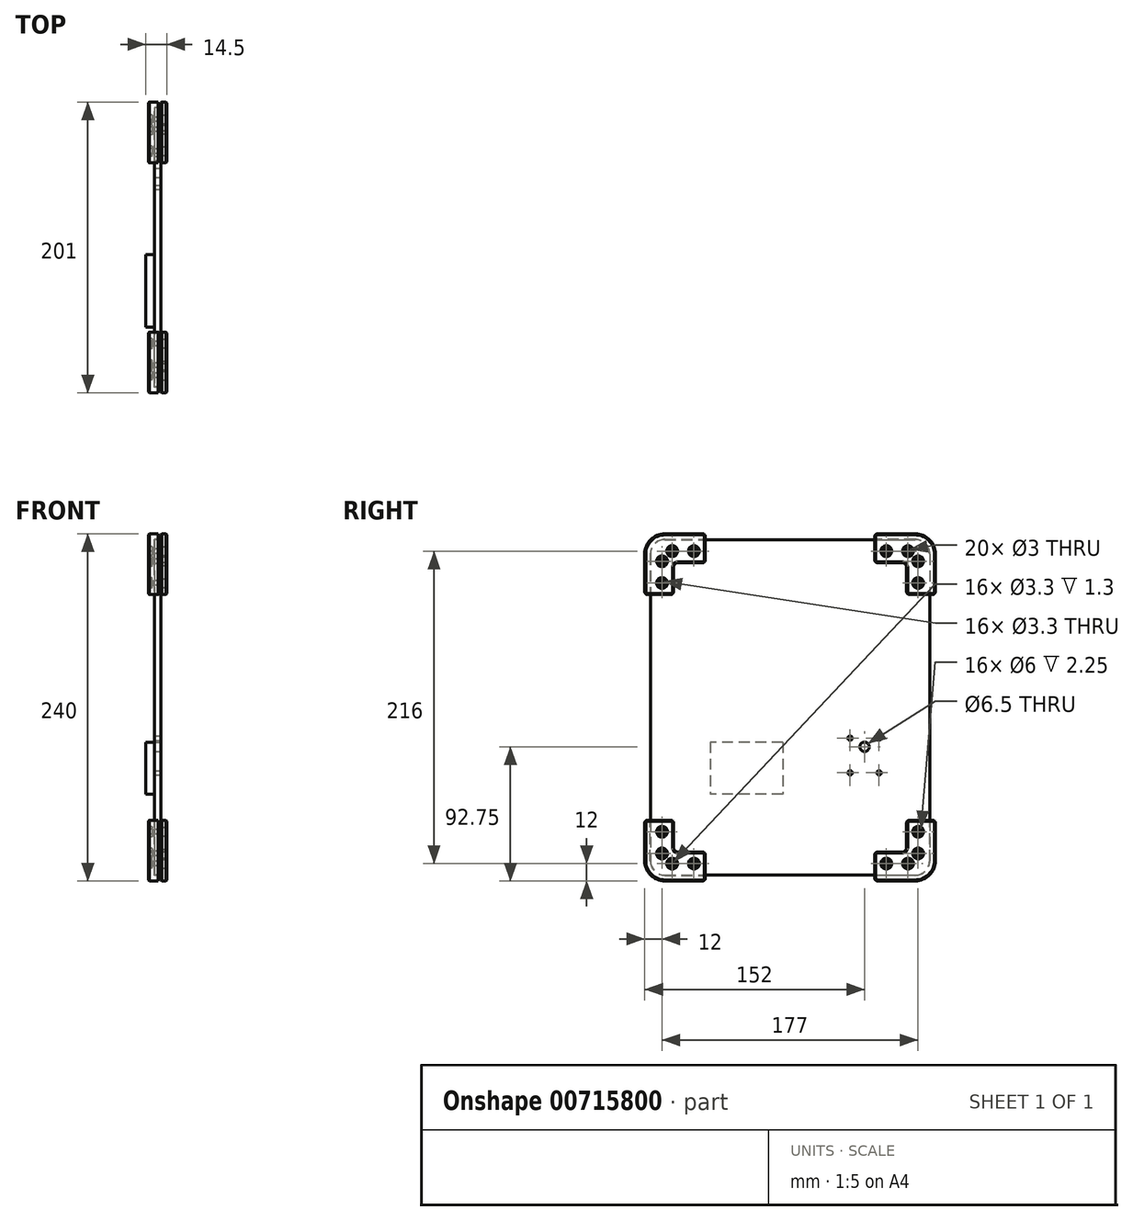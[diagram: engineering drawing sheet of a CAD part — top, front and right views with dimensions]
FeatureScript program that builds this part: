
annotation { "Feature Type Name" : "Feature", "Feature Type Description" : "" }
export const myFeature = defineFeature(function(context is Context, id is Id, definition is map)
    precondition{}
    {
        {
            assignVariable(context, id + "F0", {"name" : "thickness", "anyValue" : 4.5});
        }
        {
            assignVariable(context, id + "F1", {"name" : "m3_printed", "anyValue" : 3.3});
        }
        {
            assignVariable(context, id + "F2", {"name" : "m3_head", "anyValue" : 6});
        }
        {
            var Q0;
            Q0=qCreatedBy(makeId("Right.planeOp"),FACE);
            var sketch = newSketch(context, id + "F3", { "sketchPlane" : qUnion([Q0])});
            skLineSegment(sketch, "E0.bottom", {"start": v(-86.5, 116) * mm, "end": v(86.5, 116) * mm});
            skLineSegment(sketch, "E0.top", {"start": v(-86.5, -116) * mm, "end": v(86.5, -116) * mm});
            skLineSegment(sketch, "E0.left", {"start": v(-96.5, 106) * mm, "end": v(-96.5, -106) * mm});
            skLineSegment(sketch, "E0.right", {"start": v(96.5, 106) * mm, "end": v(96.5, -106) * mm});
            skPoint(sketch, "E0.middle", {"position": v(0, 0) * mm});
            skPoint(sketch, "E1.visualSharp", {"position": v(-96.5, 116) * mm});
            skArc(sketch, "E1.filletArc", {"start": v(-86.5, 116) * mm, "mid": v(-93.57, 113.07) * mm, "end": v(-96.5, 106) * mm});
            skPoint(sketch, "E2.visualSharp", {"position": v(96.5, 116) * mm});
            skArc(sketch, "E2.filletArc", {"start": v(96.5, 106) * mm, "mid": v(93.57, 113.07) * mm, "end": v(86.5, 116) * mm});
            skPoint(sketch, "E3.visualSharp", {"position": v(96.5, -116) * mm});
            skArc(sketch, "E3.filletArc", {"start": v(86.5, -116) * mm, "mid": v(93.57, -113.07) * mm, "end": v(96.5, -106) * mm});
            skPoint(sketch, "E4.visualSharp", {"position": v(-96.5, -116) * mm});
            skArc(sketch, "E4.filletArc", {"start": v(-96.5, -106) * mm, "mid": v(-93.57, -113.07) * mm, "end": v(-86.5, -116) * mm});
            skSolve(sketch);
        }
        {
            var Q0;
            Q0 = qSketchRegion(id + "F3", true);
            extrude(context, id + "F4", {"entities" : qUnion([Q0]), "endBound" : BoundingType.SYMMETRIC, "depth" : (getVariable(context, 'thickness')) * mm, "offsetDistance" : 25 * mm});
        }
        {
            var Q0;
            Q0=qCreatedBy(makeId("Right.planeOp"),FACE);
            var sketch = newSketch(context, id + "F5", { "sketchPlane" : qUnion([Q0])});
            skCircle(sketch, "E5", {"center": v(-66.5, 108) * mm, "radius": 1.5 * mm});
            skCircle(sketch, "E6", {"center": v(-81.5, 108) * mm, "radius": 1.5 * mm});
            skCircle(sketch, "E7", {"center": v(-88.5, 101) * mm, "radius": 1.5 * mm});
            skCircle(sketch, "E8", {"center": v(-88.5, 86) * mm, "radius": 1.5 * mm});
            skCircle(sketch, "E9.MirrorC", {"center": v(66.5, 108) * mm, "radius": 1.5 * mm});
            skCircle(sketch, "E10.MirrorC", {"center": v(81.5, 108) * mm, "radius": 1.5 * mm});
            skCircle(sketch, "E11.MirrorC", {"center": v(88.5, 101) * mm, "radius": 1.5 * mm});
            skCircle(sketch, "E12.MirrorC", {"center": v(88.5, 86) * mm, "radius": 1.5 * mm});
            skCircle(sketch, "E13.MirrorC", {"center": v(88.5, -101) * mm, "radius": 1.5 * mm});
            skCircle(sketch, "E14.MirrorC", {"center": v(88.5, -86) * mm, "radius": 1.5 * mm});
            skCircle(sketch, "E15.MirrorC", {"center": v(81.5, -108) * mm, "radius": 1.5 * mm});
            skCircle(sketch, "E16.MirrorC", {"center": v(66.5, -108) * mm, "radius": 1.5 * mm});
            skCircle(sketch, "E17.MirrorC", {"center": v(-88.5, -86) * mm, "radius": 1.5 * mm});
            skCircle(sketch, "E18.MirrorC", {"center": v(-88.5, -101) * mm, "radius": 1.5 * mm});
            skCircle(sketch, "E19.MirrorC", {"center": v(-81.5, -108) * mm, "radius": 1.5 * mm});
            skCircle(sketch, "E20.MirrorC", {"center": v(-66.5, -108) * mm, "radius": 1.5 * mm});
            skLineSegment(sketch, "E21", {"start": v(-66.5, 108) * mm, "end": v(-81.5, 108) * mm, "construction": true});
            skLineSegment(sketch, "E22", {"start": v(-81.5, 108) * mm, "end": v(-96.5, 108) * mm, "construction": true});
            skLineSegment(sketch, "E23", {"start": v(-88.5, 86) * mm, "end": v(-88.5, 101) * mm, "construction": true});
            skLineSegment(sketch, "E24", {"start": v(-88.5, 101) * mm, "end": v(-88.5, 116) * mm, "construction": true});
            skLineSegment(sketch, "E25", {"start": v(-81.5, 108) * mm, "end": v(-81.5, 116) * mm, "construction": true});
            skLineSegment(sketch, "E26", {"start": v(-88.5, 101) * mm, "end": v(-96.5, 101) * mm, "construction": true});
            skSolve(sketch);
        }
        {
            var Q0;
            Q0 = qSketchRegion(id + "F5", true);
            extrude(context, id + "F6", {"entities" : qUnion([Q0]), "operationType" : NewBodyOperationType.REMOVE, "endBound" : BoundingType.SYMMETRIC, "depth" : 5 * mm, "offsetDistance" : 25 * mm});
        }
        {
            var Q0;
            Q0=makeQuery(id+"F4.opExtrude","CAP_FACE",FACE,{"disambiguationData":[OSD([sQuery(id+"F3.wireOp",EDGE,"E0.bottom"),sQuery(id+"F3.wireOp",EDGE,"E0.top"),sQuery(id+"F3.wireOp",EDGE,"E0.left"),sQuery(id+"F3.wireOp",EDGE,"E0.right"),sQuery(id+"F3.wireOp",EDGE,"E1.filletArc"),sQuery(id+"F3.wireOp",EDGE,"E2.filletArc"),sQuery(id+"F3.wireOp",EDGE,"E3.filletArc"),sQuery(id+"F3.wireOp",EDGE,"E4.filletArc")])],"isStart":false});
            var sketch = newSketch(context, id + "F7", { "sketchPlane" : qUnion([Q0])});
            skLineSegment(sketch, "E27", {"start": v(-58.5, 120) * mm, "end": v(-86.5, 120) * mm});
            skLineSegment(sketch, "E28", {"start": v(-100.5, 106) * mm, "end": v(-100.5, 78) * mm});
            skLineSegment(sketch, "E29", {"start": v(-100.5, 78) * mm, "end": v(-80.5, 78) * mm});
            skLineSegment(sketch, "E30", {"start": v(-80.5, 78) * mm, "end": v(-80.5, 97) * mm});
            skLineSegment(sketch, "E31", {"start": v(-77.5, 100) * mm, "end": v(-58.5, 100) * mm});
            skLineSegment(sketch, "E32", {"start": v(-58.5, 100) * mm, "end": v(-58.5, 120) * mm});
            skPoint(sketch, "E33.visualSharp", {"position": v(-100.5, 120) * mm});
            skArc(sketch, "E33.filletArc", {"start": v(-86.5, 120) * mm, "mid": v(-96.4, 115.9) * mm, "end": v(-100.5, 106) * mm});
            skPoint(sketch, "E34.visualSharp", {"position": v(-80.5, 100) * mm});
            skArc(sketch, "E34.filletArc", {"start": v(-77.5, 100) * mm, "mid": v(-79.62, 99.12) * mm, "end": v(-80.5, 97) * mm});
            skLineSegment(sketch, "E35", {"start": v(-66.5, 100) * mm, "end": v(-66.5, 108) * mm, "construction": true});
            skLineSegment(sketch, "E36", {"start": v(-66.5, 108) * mm, "end": v(-58.5, 108) * mm, "construction": true});
            skLineSegment(sketch, "E37", {"start": v(-88.5, 86) * mm, "end": v(-88.5, 78) * mm, "construction": true});
            skLineSegment(sketch, "E38", {"start": v(-88.5, 86) * mm, "end": v(-80.5, 86) * mm, "construction": true});
            skPoint(sketch, "E39", {"position": v(-81.5, 108) * mm});
            skPoint(sketch, "E40", {"position": v(-88.5, 101) * mm});
            skPoint(sketch, "E41", {"position": v(-88.5, 86) * mm});
            skPoint(sketch, "E42", {"position": v(-66.5, 108) * mm});
            skSolve(sketch);
        }
        {
            var Q0;
            Q0 = qSketchRegion(id + "F7", true);
            extrude(context, id + "F8", {"entities" : qUnion([Q0]), "depth" : 4 * mm, "offsetDistance" : 25 * mm});
        }
        {
            var Q0;
            Q0=makeQuery(id+"F4.opExtrude","CAP_FACE",FACE,{"disambiguationData":[OSD([sQuery(id+"F3.wireOp",EDGE,"E0.bottom"),sQuery(id+"F3.wireOp",EDGE,"E0.top"),sQuery(id+"F3.wireOp",EDGE,"E0.left"),sQuery(id+"F3.wireOp",EDGE,"E0.right"),sQuery(id+"F3.wireOp",EDGE,"E1.filletArc"),sQuery(id+"F3.wireOp",EDGE,"E2.filletArc"),sQuery(id+"F3.wireOp",EDGE,"E3.filletArc"),sQuery(id+"F3.wireOp",EDGE,"E4.filletArc")])],"isStart":true});
            var sketch = newSketch(context, id + "F9", { "sketchPlane" : qUnion([Q0])});
            skLineSegment(sketch, "E43.0", {"start": v(58.5, 100) * mm, "end": v(58.5, 120) * mm});
            skLineSegment(sketch, "E43.1", {"start": v(77.5, 100) * mm, "end": v(58.5, 100) * mm});
            skLineSegment(sketch, "E43.2", {"start": v(58.5, 120) * mm, "end": v(86.5, 120) * mm});
            skArc(sketch, "E43.3", {"start": v(77.5, 100) * mm, "mid": v(79.62, 99.12) * mm, "end": v(80.5, 97) * mm});
            skArc(sketch, "E43.4", {"start": v(86.5, 120) * mm, "mid": v(96.4, 115.9) * mm, "end": v(100.5, 106) * mm});
            skLineSegment(sketch, "E43.5", {"start": v(100.5, 106) * mm, "end": v(100.5, 78) * mm});
            skLineSegment(sketch, "E43.6", {"start": v(100.5, 78) * mm, "end": v(80.5, 78) * mm});
            skLineSegment(sketch, "E43.7", {"start": v(80.5, 78) * mm, "end": v(80.5, 97) * mm});
            skSolve(sketch);
        }
        {
            var Q0;
            Q0 = qSketchRegion(id + "F9", true);
            extrude(context, id + "F10", {"entities" : qUnion([Q0]), "depth" : 4 * mm, "offsetDistance" : 25 * mm});
        }
        {
            var Q0;
            Q0=makeQuery(id+"F10.opExtrude","CAP_FACE",FACE,{"disambiguationData":[OSD([sQuery(id+"F9.wireOp",EDGE,"E43.0"),sQuery(id+"F9.wireOp",EDGE,"E43.1"),sQuery(id+"F9.wireOp",EDGE,"E43.2"),sQuery(id+"F9.wireOp",EDGE,"E43.3"),sQuery(id+"F9.wireOp",EDGE,"E43.4"),sQuery(id+"F9.wireOp",EDGE,"E43.5"),sQuery(id+"F9.wireOp",EDGE,"E43.6"),sQuery(id+"F9.wireOp",EDGE,"E43.7")])],"isStart":true});
            var sketch = newSketch(context, id + "F11", { "sketchPlane" : qUnion([Q0])});
            skLineSegment(sketch, "E44.0", {"start": v(-100.5, 78) * mm, "end": v(-96.6, 78) * mm});
            skLineSegment(sketch, "E44.1", {"start": v(-58.5, 116.1) * mm, "end": v(-58.5, 120) * mm});
            skLineSegment(sketch, "E44.2", {"start": v(-58.5, 120) * mm, "end": v(-86.5, 120) * mm});
            skArc(sketch, "E44.3", {"start": v(-86.5, 120) * mm, "mid": v(-96.4, 115.9) * mm, "end": v(-100.5, 106) * mm});
            skLineSegment(sketch, "E44.4", {"start": v(-100.5, 106) * mm, "end": v(-100.5, 78) * mm});
            skLineSegment(sketch, "E45.0", {"start": v(-96.6, 106) * mm, "end": v(-96.6, 78) * mm});
            skArc(sketch, "E45.1", {"start": v(-86.5, 116.1) * mm, "mid": v(-93.64, 113.14) * mm, "end": v(-96.6, 106) * mm});
            skLineSegment(sketch, "E45.2", {"start": v(-86.5, 116.1) * mm, "end": v(-58.5, 116.1) * mm});
            skSolve(sketch);
        }
        {
            var Q0;
            Q0 = qSketchRegion(id + "F11", true);
            extrude(context, id + "F12", {"entities" : qUnion([Q0]), "operationType" : NewBodyOperationType.ADD, "depth" : 2.6 * mm, "offsetDistance" : 25 * mm});
        }
        {
            var Q0;
            Q0=makeQuery(id+"F8.opExtrude","CAP_FACE",FACE,{"disambiguationData":[OSD([sQuery(id+"F7.wireOp",EDGE,"E27"),sQuery(id+"F7.wireOp",EDGE,"E28"),sQuery(id+"F7.wireOp",EDGE,"E29"),sQuery(id+"F7.wireOp",EDGE,"E30"),sQuery(id+"F7.wireOp",EDGE,"E31"),sQuery(id+"F7.wireOp",EDGE,"E32"),sQuery(id+"F7.wireOp",EDGE,"E33.filletArc"),sQuery(id+"F7.wireOp",EDGE,"E34.filletArc")])],"isStart":false});
            var sketch = newSketch(context, id + "F13", { "sketchPlane" : qUnion([Q0])});
            skPoint(sketch, "E46", {"position": v(-81.5, 108) * mm});
            skPoint(sketch, "E47", {"position": v(-88.5, 101) * mm});
            skPoint(sketch, "E48", {"position": v(-88.5, 86) * mm});
            skPoint(sketch, "E49", {"position": v(-66.5, 108) * mm});
            skSolve(sketch);
        }
        {
            var Q0;
            Q0=sQuery(id+"F13.wireOp",VERTEX,"E48");
            var Q1;
            Q1=sQuery(id+"F13.wireOp",VERTEX,"E47");
            var Q2;
            Q2=sQuery(id+"F13.wireOp",VERTEX,"E46");
            var Q3;
            Q3=sQuery(id+"F13.wireOp",VERTEX,"E49");
            var Q4;
            Q4=makeQuery(id+"F8.opExtrude","SWEPT_BODY",BODY,{"disambiguationData":[OSD([sQuery(id+"F7.wireOp",EDGE,"E27"),sQuery(id+"F7.wireOp",EDGE,"E28"),sQuery(id+"F7.wireOp",EDGE,"E29"),sQuery(id+"F7.wireOp",EDGE,"E30"),sQuery(id+"F7.wireOp",EDGE,"E31"),sQuery(id+"F7.wireOp",EDGE,"E32"),sQuery(id+"F7.wireOp",EDGE,"E33.filletArc"),sQuery(id+"F7.wireOp",EDGE,"E34.filletArc")])]});
            hole(context, id + "F14", {"style" : HoleStyle.C_BORE, "endStyle" : HoleEndStyle.THROUGH, "holeDiameter" : (getVariable(context, 'm3_printed')) * mm, "cBoreDiameter" : (getVariable(context, 'm3_head')) * mm, "cBoreDepth" : 3 * mm, "majorDiameter" : 5 * mm, "isTappedThrough" : true, "tappedDepth" : 12 * mm, "tapClearance" : 3, "locations" : qUnion([Q0, Q1, Q2, Q3]), "scope" : qUnion([Q4])});
        }
        {
            var Q0;
            Q0=makeQuery(id+"F8.opExtrude","SWEPT_EDGE",EDGE,{"disambiguationData":[OSD([sQuery(id+"F7.wireOp",EDGE,"E31"),sQuery(id+"F7.wireOp",EDGE,"E32")])]});
            var Q1;
            Q1=makeQuery(id+"F8.opExtrude","SWEPT_EDGE",EDGE,{"disambiguationData":[OSD([sQuery(id+"F7.wireOp",EDGE,"E29"),sQuery(id+"F7.wireOp",EDGE,"E30")])]});
            var Q2;
            Q2=makeQuery(id+"F8.opExtrude","SWEPT_EDGE",EDGE,{"disambiguationData":[OSD([sQuery(id+"F7.wireOp",EDGE,"E27"),sQuery(id+"F7.wireOp",EDGE,"E32")])]});
            var Q3;
            Q3=makeQuery(id+"F8.opExtrude","SWEPT_EDGE",EDGE,{"disambiguationData":[OSD([sQuery(id+"F7.wireOp",EDGE,"E28"),sQuery(id+"F7.wireOp",EDGE,"E29")])]});
            fillet(context, id + "F15", {"entities" : qUnion([Q0, Q1, Q2, Q3]), "radius" : 2 * mm, "tangentPropagation" : true, "allowEdgeOverflow" : false});
        }
        {
            var Q0;
            Q0=makeQuery(id+"F8.opExtrude","CAP_FACE",FACE,{"disambiguationData":[OSD([sQuery(id+"F7.wireOp",EDGE,"E27"),sQuery(id+"F7.wireOp",EDGE,"E28"),sQuery(id+"F7.wireOp",EDGE,"E29"),sQuery(id+"F7.wireOp",EDGE,"E30"),sQuery(id+"F7.wireOp",EDGE,"E31"),sQuery(id+"F7.wireOp",EDGE,"E32"),sQuery(id+"F7.wireOp",EDGE,"E33.filletArc"),sQuery(id+"F7.wireOp",EDGE,"E34.filletArc")])],"isStart":false});
            chamfer(context, id + "F16", {"entities" : qUnion([Q0]), "width" : .75 * mm, "tangentPropagation" : true});
        }
        {
            var Q0;
            Q0=makeQuery(id+"F8.opExtrude","CAP_FACE",FACE,{"disambiguationData":[OSD([sQuery(id+"F7.wireOp",EDGE,"E27"),sQuery(id+"F7.wireOp",EDGE,"E28"),sQuery(id+"F7.wireOp",EDGE,"E29"),sQuery(id+"F7.wireOp",EDGE,"E30"),sQuery(id+"F7.wireOp",EDGE,"E31"),sQuery(id+"F7.wireOp",EDGE,"E32"),sQuery(id+"F7.wireOp",EDGE,"E33.filletArc"),sQuery(id+"F7.wireOp",EDGE,"E34.filletArc")])],"isStart":true});
            chamfer(context, id + "F17", {"entities" : qUnion([Q0]), "width" : .5 * mm, "tangentPropagation" : true});
        }
        {
            var Q0;
            Q0=makeQuery(id+"F10.opExtrude","CAP_FACE",FACE,{"disambiguationData":[OSD([sQuery(id+"F9.wireOp",EDGE,"E43.0"),sQuery(id+"F9.wireOp",EDGE,"E43.1"),sQuery(id+"F9.wireOp",EDGE,"E43.2"),sQuery(id+"F9.wireOp",EDGE,"E43.3"),sQuery(id+"F9.wireOp",EDGE,"E43.4"),sQuery(id+"F9.wireOp",EDGE,"E43.5"),sQuery(id+"F9.wireOp",EDGE,"E43.6"),sQuery(id+"F9.wireOp",EDGE,"E43.7")])],"isStart":true});
            var sketch = newSketch(context, id + "F18", { "sketchPlane" : qUnion([Q0])});
            skPoint(sketch, "E50", {"position": v(-88.5, 86) * mm});
            skPoint(sketch, "E51", {"position": v(-88.5, 101) * mm});
            skPoint(sketch, "E52", {"position": v(-81.5, 108) * mm});
            skPoint(sketch, "E53", {"position": v(-66.5, 108) * mm});
            skSolve(sketch);
        }
        {
            var Q0;
            Q0=sQuery(id+"F18.wireOp",VERTEX,"E51");
            var Q1;
            Q1=sQuery(id+"F18.wireOp",VERTEX,"E50");
            var Q2;
            Q2=sQuery(id+"F18.wireOp",VERTEX,"E52");
            var Q3;
            Q3=sQuery(id+"F18.wireOp",VERTEX,"E53");
            var Q4;
            Q4=makeQuery(id+"F10.opExtrude","SWEPT_BODY",BODY,{"disambiguationData":[OSD([sQuery(id+"F9.wireOp",EDGE,"E43.0"),sQuery(id+"F9.wireOp",EDGE,"E43.1"),sQuery(id+"F9.wireOp",EDGE,"E43.2"),sQuery(id+"F9.wireOp",EDGE,"E43.3"),sQuery(id+"F9.wireOp",EDGE,"E43.4"),sQuery(id+"F9.wireOp",EDGE,"E43.5"),sQuery(id+"F9.wireOp",EDGE,"E43.6"),sQuery(id+"F9.wireOp",EDGE,"E43.7")])]});
            hole(context, id + "F19", {"style" : HoleStyle.SIMPLE, "endStyle" : HoleEndStyle.THROUGH, "holeDiameter" : (getVariable(context, 'm3_printed')) * mm, "majorDiameter" : 5 * mm, "isTappedThrough" : true, "tappedDepth" : 12 * mm, "tapClearance" : 3, "locations" : qUnion([Q0, Q1, Q2, Q3]), "scope" : qUnion([Q4])});
        }
        {
            var Q0;
            Q0=makeQuery(id+"F10.opExtrude","CAP_FACE",FACE,{"disambiguationData":[OSD([sQuery(id+"F9.wireOp",EDGE,"E43.0"),sQuery(id+"F9.wireOp",EDGE,"E43.1"),sQuery(id+"F9.wireOp",EDGE,"E43.2"),sQuery(id+"F9.wireOp",EDGE,"E43.3"),sQuery(id+"F9.wireOp",EDGE,"E43.4"),sQuery(id+"F9.wireOp",EDGE,"E43.5"),sQuery(id+"F9.wireOp",EDGE,"E43.6"),sQuery(id+"F9.wireOp",EDGE,"E43.7")])],"isStart":false});
            var sketch = newSketch(context, id + "F20", { "sketchPlane" : qUnion([Q0])});
            skCircle(sketch, "E54.cCircle", {"center": v(88.5, 86) * mm, "radius": 3.46 * mm, "construction": true});
            skLineSegment(sketch, "E54.0", {"start": v(85.5, 87.73) * mm, "end": v(88.5, 89.46) * mm});
            skLineSegment(sketch, "E54.1", {"start": v(88.5, 89.46) * mm, "end": v(91.5, 87.73) * mm});
            skLineSegment(sketch, "E54.2", {"start": v(91.5, 87.73) * mm, "end": v(91.5, 84.27) * mm});
            skLineSegment(sketch, "E54.3", {"start": v(91.5, 84.27) * mm, "end": v(88.5, 82.54) * mm});
            skLineSegment(sketch, "E54.4", {"start": v(88.5, 82.54) * mm, "end": v(85.5, 84.27) * mm});
            skLineSegment(sketch, "E54.5", {"start": v(85.5, 84.27) * mm, "end": v(85.5, 87.73) * mm});
            skCircle(sketch, "E55.cCircle", {"center": v(88.5, 101) * mm, "radius": 3.46 * mm, "construction": true});
            skLineSegment(sketch, "E55.0", {"start": v(85.5, 99.27) * mm, "end": v(85.5, 102.73) * mm});
            skLineSegment(sketch, "E55.1", {"start": v(85.5, 102.73) * mm, "end": v(88.5, 104.46) * mm});
            skLineSegment(sketch, "E55.2", {"start": v(88.5, 104.46) * mm, "end": v(91.5, 102.73) * mm});
            skLineSegment(sketch, "E55.3", {"start": v(91.5, 102.73) * mm, "end": v(91.5, 99.27) * mm});
            skLineSegment(sketch, "E55.4", {"start": v(91.5, 99.27) * mm, "end": v(88.5, 97.54) * mm});
            skLineSegment(sketch, "E55.5", {"start": v(88.5, 97.54) * mm, "end": v(85.5, 99.27) * mm});
            skCircle(sketch, "E56.cCircle", {"center": v(81.5, 108) * mm, "radius": 3.46 * mm, "construction": true});
            skLineSegment(sketch, "E56.0", {"start": v(79.77, 105) * mm, "end": v(78.04, 108) * mm});
            skLineSegment(sketch, "E56.1", {"start": v(78.04, 108) * mm, "end": v(79.77, 111) * mm});
            skLineSegment(sketch, "E56.2", {"start": v(79.77, 111) * mm, "end": v(83.23, 111) * mm});
            skLineSegment(sketch, "E56.3", {"start": v(83.23, 111) * mm, "end": v(84.96, 108) * mm});
            skLineSegment(sketch, "E56.4", {"start": v(84.96, 108) * mm, "end": v(83.23, 105) * mm});
            skLineSegment(sketch, "E56.5", {"start": v(83.23, 105) * mm, "end": v(79.77, 105) * mm});
            skCircle(sketch, "E57.cCircle", {"center": v(66.5, 108) * mm, "radius": 3.46 * mm, "construction": true});
            skLineSegment(sketch, "E57.0", {"start": v(68.23, 105) * mm, "end": v(64.77, 105) * mm});
            skLineSegment(sketch, "E57.1", {"start": v(64.77, 105) * mm, "end": v(63.04, 108) * mm});
            skLineSegment(sketch, "E57.2", {"start": v(63.04, 108) * mm, "end": v(64.77, 111) * mm});
            skLineSegment(sketch, "E57.3", {"start": v(64.77, 111) * mm, "end": v(68.23, 111) * mm});
            skLineSegment(sketch, "E57.4", {"start": v(68.23, 111) * mm, "end": v(69.96, 108) * mm});
            skLineSegment(sketch, "E57.5", {"start": v(69.96, 108) * mm, "end": v(68.23, 105) * mm});
            skSolve(sketch);
        }
        {
            var Q0;
            Q0 = qSketchRegion(id + "F20", true);
            extrude(context, id + "F21", {"entities" : qUnion([Q0]), "operationType" : NewBodyOperationType.REMOVE, "oppositeDirection" : true, "depth" : 2.5 * mm, "offsetDistance" : 25 * mm});
        }
        {
            var Q0;
            Q0=makeQuery(id+"F10.opExtrude","SWEPT_EDGE",EDGE,{"disambiguationData":[OSD([sQuery(id+"F9.wireOp",EDGE,"E43.0"),sQuery(id+"F9.wireOp",EDGE,"E43.1")])]});
            var Q1;
            Q1=makeQuery(id+"F10.opExtrude","SWEPT_EDGE",EDGE,{"disambiguationData":[OSD([sQuery(id+"F9.wireOp",EDGE,"E43.6"),sQuery(id+"F9.wireOp",EDGE,"E43.7")])]});
            var Q2;
            Q2=makeQuery(id+"F12.boolean.opBoolean","MERGE",EDGE,{"derivedFrom":[makeQuery(id+"F10.opExtrude","SWEPT_EDGE",EDGE,{"disambiguationData":[OSD([sQuery(id+"F9.wireOp",EDGE,"E43.5"),sQuery(id+"F9.wireOp",EDGE,"E43.6")])]}),makeQuery(id+"F12.opExtrude","SWEPT_EDGE",EDGE,{"disambiguationData":[OSD([sQuery(id+"F11.wireOp",EDGE,"E44.0"),sQuery(id+"F11.wireOp",EDGE,"E44.4")])]})]});
            var Q3;
            Q3=makeQuery(id+"F12.boolean.opBoolean","MERGE",EDGE,{"derivedFrom":[makeQuery(id+"F10.opExtrude","SWEPT_EDGE",EDGE,{"disambiguationData":[OSD([sQuery(id+"F9.wireOp",EDGE,"E43.0"),sQuery(id+"F9.wireOp",EDGE,"E43.2")])]}),makeQuery(id+"F12.opExtrude","SWEPT_EDGE",EDGE,{"disambiguationData":[OSD([sQuery(id+"F11.wireOp",EDGE,"E44.1"),sQuery(id+"F11.wireOp",EDGE,"E44.2")])]})]});
            fillet(context, id + "F22", {"entities" : qUnion([Q0, Q1, Q2, Q3]), "radius" : 2 * mm, "tangentPropagation" : true, "allowEdgeOverflow" : false});
        }
        {
            var Q0;
            Q0=makeQuery(id+"F10.opExtrude","CAP_FACE",FACE,{"disambiguationData":[OSD([sQuery(id+"F9.wireOp",EDGE,"E43.0"),sQuery(id+"F9.wireOp",EDGE,"E43.1"),sQuery(id+"F9.wireOp",EDGE,"E43.2"),sQuery(id+"F9.wireOp",EDGE,"E43.3"),sQuery(id+"F9.wireOp",EDGE,"E43.4"),sQuery(id+"F9.wireOp",EDGE,"E43.5"),sQuery(id+"F9.wireOp",EDGE,"E43.6"),sQuery(id+"F9.wireOp",EDGE,"E43.7")])],"isStart":false});
            chamfer(context, id + "F23", {"entities" : qUnion([Q0]), "width" : 0.5 * mm, "tangentPropagation" : true});
        }
        {
            var Q0;
            Q0=makeQuery(id+"F21.boolean.opBoolean","COPY",FACE,{"derivedFrom":makeQuery(id+"F21.opExtrude","CAP_FACE",FACE,{"disambiguationData":[OSD([sQuery(id+"F20.wireOp",EDGE,"E54.0"),sQuery(id+"F20.wireOp",EDGE,"E54.1"),sQuery(id+"F20.wireOp",EDGE,"E54.2"),sQuery(id+"F20.wireOp",EDGE,"E54.3"),sQuery(id+"F20.wireOp",EDGE,"E54.4"),sQuery(id+"F20.wireOp",EDGE,"E54.5")])],"isStart":false})});
            var sketch = newSketch(context, id + "F24", { "sketchPlane" : qUnion([Q0])});
            skCircle(sketch, "E58", {"center": v(88.5, 86) * mm, "radius": 1.65 * mm});
            skCircle(sketch, "E59", {"center": v(88.5, 101) * mm, "radius": 1.65 * mm});
            skCircle(sketch, "E60", {"center": v(81.5, 108) * mm, "radius": 1.65 * mm});
            skCircle(sketch, "E61", {"center": v(66.5, 108) * mm, "radius": 1.65 * mm});
            skSolve(sketch);
        }
        {
            var Q0;
            Q0 = qSketchRegion(id + "F24", true);
            extrude(context, id + "F25", {"entities" : qUnion([Q0]), "operationType" : NewBodyOperationType.ADD, "oppositeDirection" : true, "depth" : .2 * mm, "offsetDistance" : 25 * mm});
        }
        {
            var Q0;
            Q0=makeQuery(id+"F8.opExtrude","SWEPT_BODY",BODY,{"disambiguationData":[OSD([sQuery(id+"F7.wireOp",EDGE,"E27"),sQuery(id+"F7.wireOp",EDGE,"E28"),sQuery(id+"F7.wireOp",EDGE,"E29"),sQuery(id+"F7.wireOp",EDGE,"E30"),sQuery(id+"F7.wireOp",EDGE,"E31"),sQuery(id+"F7.wireOp",EDGE,"E32"),sQuery(id+"F7.wireOp",EDGE,"E33.filletArc"),sQuery(id+"F7.wireOp",EDGE,"E34.filletArc")])]});
            var Q1;
            Q1=makeQuery(id+"F10.opExtrude","SWEPT_BODY",BODY,{"disambiguationData":[OSD([sQuery(id+"F9.wireOp",EDGE,"E43.0"),sQuery(id+"F9.wireOp",EDGE,"E43.1"),sQuery(id+"F9.wireOp",EDGE,"E43.2"),sQuery(id+"F9.wireOp",EDGE,"E43.3"),sQuery(id+"F9.wireOp",EDGE,"E43.4"),sQuery(id+"F9.wireOp",EDGE,"E43.5"),sQuery(id+"F9.wireOp",EDGE,"E43.6"),sQuery(id+"F9.wireOp",EDGE,"E43.7")])]});
            var Q2;
            Q2=qCreatedBy(makeId("Front.planeOp"),FACE);
            mirror(context, id + "F26", {"entities" : qUnion([Q0, Q1]), "mirrorPlane" : qUnion([Q2])});
        }
        {
            var Q0;
            Q0=makeQuery(id+"F8.opExtrude","SWEPT_BODY",BODY,{"disambiguationData":[OSD([sQuery(id+"F7.wireOp",EDGE,"E27"),sQuery(id+"F7.wireOp",EDGE,"E28"),sQuery(id+"F7.wireOp",EDGE,"E29"),sQuery(id+"F7.wireOp",EDGE,"E30"),sQuery(id+"F7.wireOp",EDGE,"E31"),sQuery(id+"F7.wireOp",EDGE,"E32"),sQuery(id+"F7.wireOp",EDGE,"E33.filletArc"),sQuery(id+"F7.wireOp",EDGE,"E34.filletArc")])]});
            var Q1;
            Q1=makeQuery(id+"F10.opExtrude","SWEPT_BODY",BODY,{"disambiguationData":[OSD([sQuery(id+"F9.wireOp",EDGE,"E43.0"),sQuery(id+"F9.wireOp",EDGE,"E43.1"),sQuery(id+"F9.wireOp",EDGE,"E43.2"),sQuery(id+"F9.wireOp",EDGE,"E43.3"),sQuery(id+"F9.wireOp",EDGE,"E43.4"),sQuery(id+"F9.wireOp",EDGE,"E43.5"),sQuery(id+"F9.wireOp",EDGE,"E43.6"),sQuery(id+"F9.wireOp",EDGE,"E43.7")])]});
            var Q2;
            Q2=makeQuery(id+"F26.opPattern","COPY",BODY,{"derivedFrom":makeQuery(id+"F8.opExtrude","SWEPT_BODY",BODY,{"disambiguationData":[OSD([sQuery(id+"F7.wireOp",EDGE,"E27"),sQuery(id+"F7.wireOp",EDGE,"E28"),sQuery(id+"F7.wireOp",EDGE,"E29"),sQuery(id+"F7.wireOp",EDGE,"E30"),sQuery(id+"F7.wireOp",EDGE,"E31"),sQuery(id+"F7.wireOp",EDGE,"E32"),sQuery(id+"F7.wireOp",EDGE,"E33.filletArc"),sQuery(id+"F7.wireOp",EDGE,"E34.filletArc")])]}),"instanceName":"1"});
            var Q3;
            Q3=makeQuery(id+"F26.opPattern","COPY",BODY,{"derivedFrom":makeQuery(id+"F10.opExtrude","SWEPT_BODY",BODY,{"disambiguationData":[OSD([sQuery(id+"F9.wireOp",EDGE,"E43.0"),sQuery(id+"F9.wireOp",EDGE,"E43.1"),sQuery(id+"F9.wireOp",EDGE,"E43.2"),sQuery(id+"F9.wireOp",EDGE,"E43.3"),sQuery(id+"F9.wireOp",EDGE,"E43.4"),sQuery(id+"F9.wireOp",EDGE,"E43.5"),sQuery(id+"F9.wireOp",EDGE,"E43.6"),sQuery(id+"F9.wireOp",EDGE,"E43.7")])]}),"instanceName":"1"});
            var Q4;
            Q4=qCreatedBy(makeId("Top.planeOp"),FACE);
            mirror(context, id + "F27", {"entities" : qUnion([Q0, Q1, Q2, Q3]), "mirrorPlane" : qUnion([Q4])});
        }
        {
            var Q0;
            Q0=makeQuery(id+"F4.opExtrude","CAP_FACE",FACE,{"disambiguationData":[OSD([sQuery(id+"F3.wireOp",EDGE,"E0.bottom"),sQuery(id+"F3.wireOp",EDGE,"E0.top"),sQuery(id+"F3.wireOp",EDGE,"E0.left"),sQuery(id+"F3.wireOp",EDGE,"E0.right"),sQuery(id+"F3.wireOp",EDGE,"E1.filletArc"),sQuery(id+"F3.wireOp",EDGE,"E2.filletArc"),sQuery(id+"F3.wireOp",EDGE,"E3.filletArc"),sQuery(id+"F3.wireOp",EDGE,"E4.filletArc")])],"isStart":true});
            var sketch = newSketch(context, id + "F28", { "sketchPlane" : qUnion([Q0])});
            skLineSegment(sketch, "E62.bottom", {"start": v(5, -24) * mm, "end": v(55, -24) * mm});
            skLineSegment(sketch, "E62.top", {"start": v(5, -60) * mm, "end": v(55, -60) * mm});
            skLineSegment(sketch, "E62.left", {"start": v(5, -24) * mm, "end": v(5, -60) * mm});
            skLineSegment(sketch, "E62.right", {"start": v(55, -24) * mm, "end": v(55, -60) * mm});
            skPoint(sketch, "E62.middle", {"position": v(30, -42) * mm});
            skSolve(sketch);
        }
        {
            var Q0;
            Q0 = qSketchRegion(id + "F28", true);
            extrude(context, id + "F29", {"entities" : qUnion([Q0]), "depth" : 6 * mm, "offsetDistance" : 25 * mm});
        }
        {
            var Q0;
            Q0=makeQuery(id+"F4.opExtrude","CAP_FACE",FACE,{"disambiguationData":[OSD([sQuery(id+"F3.wireOp",EDGE,"E0.bottom"),sQuery(id+"F3.wireOp",EDGE,"E0.top"),sQuery(id+"F3.wireOp",EDGE,"E0.left"),sQuery(id+"F3.wireOp",EDGE,"E0.right"),sQuery(id+"F3.wireOp",EDGE,"E1.filletArc"),sQuery(id+"F3.wireOp",EDGE,"E2.filletArc"),sQuery(id+"F3.wireOp",EDGE,"E3.filletArc"),sQuery(id+"F3.wireOp",EDGE,"E4.filletArc")])],"isStart":false});
            var sketch = newSketch(context, id + "F30", { "sketchPlane" : qUnion([Q0])});
            skCircle(sketch, "E63", {"center": v(51.5, -27.25) * mm, "radius": 3.25 * mm});
            skSolve(sketch);
        }
        {
            var Q0;
            Q0 = qSketchRegion(id + "F30", true);
            extrude(context, id + "F31", {"entities" : qUnion([Q0]), "operationType" : NewBodyOperationType.REMOVE, "endBound" : BoundingType.THROUGH_ALL, "oppositeDirection" : true, "depth" : 25 * mm, "offsetDistance" : 25 * mm});
        }
        {
            var Q0;
            Q0=makeQuery(id+"F4.opExtrude","CAP_FACE",FACE,{"disambiguationData":[OSD([sQuery(id+"F3.wireOp",EDGE,"E0.bottom"),sQuery(id+"F3.wireOp",EDGE,"E0.top"),sQuery(id+"F3.wireOp",EDGE,"E0.left"),sQuery(id+"F3.wireOp",EDGE,"E0.right"),sQuery(id+"F3.wireOp",EDGE,"E1.filletArc"),sQuery(id+"F3.wireOp",EDGE,"E2.filletArc"),sQuery(id+"F3.wireOp",EDGE,"E3.filletArc"),sQuery(id+"F3.wireOp",EDGE,"E4.filletArc")])],"isStart":false});
            var sketch = newSketch(context, id + "F32", { "sketchPlane" : qUnion([Q0])});
            skCircle(sketch, "E64", {"center": v(41.5, -45.25) * mm, "radius": 1.5 * mm});
            skLineSegment(sketch, "E65", {"start": v(51.5, -27.25) * mm, "end": v(51.5, -78.37) * mm, "construction": true});
            skLineSegment(sketch, "E66", {"start": v(45.67, -33.25) * mm, "end": v(32.76, -33.25) * mm, "construction": true});
            skCircle(sketch, "E67.MirrorC", {"center": v(41.5, -21.25) * mm, "radius": 1.5 * mm});
            skCircle(sketch, "E68.MirrorC", {"center": v(61.5, -21.25) * mm, "radius": 1.5 * mm});
            skCircle(sketch, "E69.MirrorC", {"center": v(61.5, -45.25) * mm, "radius": 1.5 * mm});
            skSolve(sketch);
        }
        {
            var Q0;
            Q0 = qSketchRegion(id + "F32", true);
            extrude(context, id + "F33", {"entities" : qUnion([Q0]), "operationType" : NewBodyOperationType.REMOVE, "endBound" : BoundingType.THROUGH_ALL, "oppositeDirection" : true, "depth" : 25 * mm, "offsetDistance" : 25 * mm});
        }
    });
